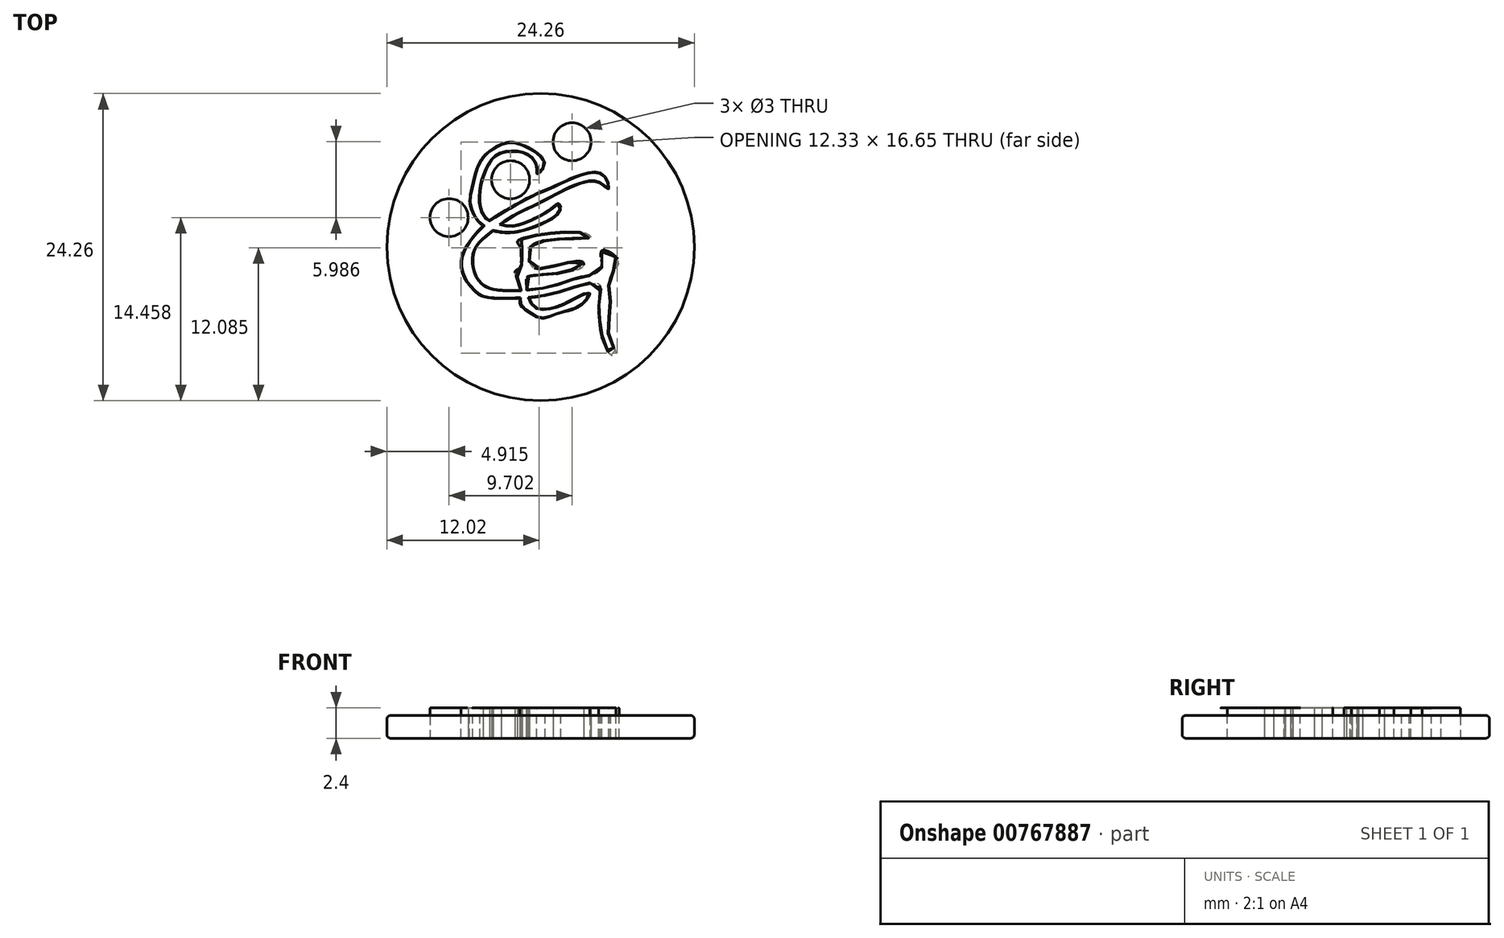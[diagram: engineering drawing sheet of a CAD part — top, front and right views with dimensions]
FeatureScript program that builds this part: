
annotation { "Feature Type Name" : "Feature", "Feature Type Description" : "" }
export const myFeature = defineFeature(function(context is Context, id is Id, definition is map)
    precondition{}
    {
        {
            var Q0;
            Q0=qCreatedBy(makeId("Top.planeOp"),FACE);
            var sketch = newSketch(context, id + "F0", { "sketchPlane" : qUnion([Q0])});
            skCircle(sketch, "E0", {"center": v(0, 0) * mm, "radius": 12.13 * mm});
            skCircle(sketch, "E1", {"center": v(-7.22, 2.33) * mm, "radius": 1.5 * mm});
            skCircle(sketch, "E2.1.0.0", {"center": v(-2.36, 5.32) * mm, "radius": 1.5 * mm});
            skCircle(sketch, "E2.2.0.0", {"center": v(2.49, 8.31) * mm, "radius": 1.5 * mm});
            skLineSegment(sketch, "E2.direction1", {"start": v(-7.22, 2.33) * mm, "end": v(-2.36, 5.32) * mm, "construction": true});
            skPoint(sketch, "E3.20.internal.snap0", {"position": v(-4.79, 3.82) * mm});
            skFitSpline(sketch, "E3", {"points": [v(-0.27, 5.8) * mm, v(0.34, 6.54) * mm, v(-0.62, 7.67) * mm, v(-1.5, 8.11) * mm, v(-2.55, 8.28) * mm, v(-4.1, 7.53) * mm, v(-4.89, 6.55) * mm, v(-5.26, 5.43) * mm, v(-5.52, 4.2) * mm, v(-5.57, 3.34) * mm, v(-4.72, 1.82) * mm, v(-2.7, 1.13) * mm, v(-0.35, 1.63) * mm, v(1.54, 2.89) * mm, v(1.42, 3.44) * mm, v(0.9, 3.08) * mm, v(-0.43, 2.3) * mm, v(-2.31, 1.67) * mm, v(-3.5, 1.92) * mm, v(-4.44, 2.44) * mm, v(-4.79, 4.2) * mm, v(-4.34, 6.01) * mm, v(-3.45, 7.26) * mm, v(-2.08, 7.54) * mm, v(-1.07, 7.32) * mm, v(-0.33, 6.4) * mm, v(-0.27, 5.8) * mm]});
            skFitSpline(sketch, "E4", {"points": [v(5.62, -8.55) * mm, v(5.96, -8.32) * mm, v(5.51, -7.5) * mm, v(5.44, -5.47) * mm, v(5.5, -4.03) * mm, v(5.54, -2.2) * mm, v(6.18, -1.14) * mm, v(4.94, -0.23) * mm, v(4.75, -0.7) * mm, v(4.84, -1.47) * mm, v(4.33, -2.02) * mm, v(2.9, -2.42) * mm, v(1.63, -2.84) * mm, v(0, -3.25) * mm, v(-2.31, -3.42) * mm, v(-4.24, -3.14) * mm, v(-5.19, -2) * mm, v(-5.23, -0.31) * mm, v(-4.32, 0.8) * mm, v(-2.31, 2.34) * mm, v(-0.27, 3.37) * mm, v(1.6, 4.35) * mm, v(3.38, 5.09) * mm, v(4.73, 5.03) * mm, v(5.38, 4.6) * mm, v(4.83, 5.8) * mm, v(1.54, 5.02) * mm, v(0.3, 4.49) * mm, v(-0.99, 3.9) * mm, v(-2.83, 2.87) * mm, v(-3.92, 2.18) * mm, v(-5.17, 1.02) * mm, v(-5.9, 0) * mm, v(-6.26, -1.03) * mm, v(-6.06, -2.32) * mm, v(-5.23, -3.45) * mm, v(-4.44, -3.94) * mm, v(-1.6, -4.03) * mm, v(1.43, -3.58) * mm, v(4.57, -2.9) * mm, v(4.6, -4.2) * mm, v(4.66, -5.96) * mm, v(4.86, -7.19) * mm, v(5.62, -8.55) * mm]});
            skFitSpline(sketch, "E5", {"points": [v(3.93, 0.77) * mm, v(2.32, 0.66) * mm, v(0.7, 0.53) * mm, v(-0.8, 0) * mm, v(-0.78, -1.37) * mm, v(0, -1.68) * mm, v(3.32, -1.16) * mm, v(3.23, -1.66) * mm, v(2.2, -1.85) * mm, v(1.22, -2.12) * mm, v(-0.87, -2.28) * mm, v(-1.13, -2.63) * mm, v(-0.75, -4.35) * mm, v(0, -4.89) * mm, v(1.52, -4.6) * mm, v(3.04, -3.85) * mm, v(3.88, -3.61) * mm, v(3.18, -4.6) * mm, v(1.49, -5.22) * mm, v(0, -5.63) * mm, v(-0.92, -5.13) * mm, v(-1.6, -4.56) * mm, v(-1.6, -3.13) * mm, v(-2, -1.92) * mm, v(-1.6, -1.59) * mm, v(-1.6, 0) * mm, v(-1.84, 0.36) * mm, v(-1.6, 0.63) * mm, v(3.48, 1.12) * mm, v(3.93, 0.77) * mm]});
            skSolve(sketch);
        }
        {
            var Q0;
            Q0=makeQuery(id+"F0.imprint","IMPRINT",FACE,{"disambiguationData":[TD([[makeQuery(id+"F0.imprint","IMPRINT",EDGE,{"derivedFrom":sQuery(id+"F0.wireOp",EDGE,"E2.1.0.0")}),1.0]])]});
            var Q1;
            Q1=makeQuery(id+"F0.imprint","IMPRINT",FACE,{"disambiguationData":[TD([[makeQuery(id+"F0.imprint","IMPRINT",EDGE,{"derivedFrom":sQuery(id+"F0.wireOp",EDGE,"E1")}),1.0]])]});
            var Q2;
            Q2=makeQuery(id+"F0.imprint","IMPRINT",FACE,{"disambiguationData":[TD([[makeQuery(id+"F0.imprint","IMPRINT",EDGE,{"derivedFrom":sQuery(id+"F0.wireOp",EDGE,"E2.2.0.0")}),1.0]])]});
            var Q3;
            {var subQ0=sQuery(id+"F0.wireOp",EDGE,"E4");var subQ1=sQuery(id+"F0.wireOp",EDGE,"E3");var subQ2=makeQuery(id+"F0.imprint","INTERSECT",VERTEX,{"disambiguationData":[OD(2.0)],"derivedFrom":[subQ1,subQ0]});Q3=makeQuery(id+"F0.imprint","IMPRINT",FACE,{"disambiguationData":[TD([[makeQuery(id+"F0.imprint","IMPRINT",EDGE,{"disambiguationData":[TD([[subQ2,-1.0]])],"derivedFrom":subQ1}),-1.0]])]});}
            var Q4;
            {var subQ0=sQuery(id+"F0.wireOp",EDGE,"E4");var subQ1=sQuery(id+"F0.wireOp",EDGE,"E3");var subQ2=makeQuery(id+"F0.imprint","INTERSECT",VERTEX,{"disambiguationData":[OD(0.0)],"derivedFrom":[subQ1,subQ0]});Q4=makeQuery(id+"F0.imprint","IMPRINT",FACE,{"disambiguationData":[TD([[makeQuery(id+"F0.imprint","IMPRINT",EDGE,{"disambiguationData":[TD([[subQ2,-1.0]])],"derivedFrom":subQ1}),1.0]])]});}
            var Q5;
            {var subQ0=sQuery(id+"F0.wireOp",EDGE,"E4");var subQ1=sQuery(id+"F0.wireOp",EDGE,"E3");var subQ2=makeQuery(id+"F0.imprint","INTERSECT",VERTEX,{"disambiguationData":[OD(0.0)],"derivedFrom":[subQ1,subQ0]});Q5=makeQuery(id+"F0.imprint","IMPRINT",FACE,{"disambiguationData":[TD([[makeQuery(id+"F0.imprint","IMPRINT",EDGE,{"disambiguationData":[TD([[subQ2,1.0]])],"derivedFrom":subQ1}),1.0]])]});}
            var Q6;
            {var subQ0=sQuery(id+"F0.wireOp",EDGE,"E4");var subQ1=sQuery(id+"F0.wireOp",EDGE,"E3");var subQ2=makeQuery(id+"F0.imprint","INTERSECT",VERTEX,{"disambiguationData":[OD(1.0)],"derivedFrom":[subQ1,subQ0]});Q6=makeQuery(id+"F0.imprint","IMPRINT",FACE,{"disambiguationData":[TD([[makeQuery(id+"F0.imprint","IMPRINT",EDGE,{"disambiguationData":[TD([[subQ2,1.0]])],"derivedFrom":subQ1}),1.0]])]});}
            var Q7;
            {var subQ0=sQuery(id+"F0.wireOp",EDGE,"E4");var subQ1=sQuery(id+"F0.wireOp",EDGE,"E3");var subQ2=makeQuery(id+"F0.imprint","INTERSECT",VERTEX,{"disambiguationData":[OD(0.0)],"derivedFrom":[subQ1,subQ0]});Q7=makeQuery(id+"F0.imprint","IMPRINT",FACE,{"disambiguationData":[TD([[makeQuery(id+"F0.imprint","IMPRINT",EDGE,{"disambiguationData":[TD([[subQ2,1.0]])],"derivedFrom":subQ1}),-1.0]])]});}
            var Q8;
            {var subQ0=sQuery(id+"F0.wireOp",EDGE,"E5");var subQ1=sQuery(id+"F0.wireOp",EDGE,"E4");var subQ2=makeQuery(id+"F0.imprint","INTERSECT",VERTEX,{"disambiguationData":[OD(0.0)],"derivedFrom":[subQ1,subQ0]});Q8=makeQuery(id+"F0.imprint","IMPRINT",FACE,{"disambiguationData":[TD([[makeQuery(id+"F0.imprint","IMPRINT",EDGE,{"disambiguationData":[TD([[subQ2,1.0]])],"derivedFrom":subQ1}),-1.0]])]});}
            var Q9;
            {var subQ0=sQuery(id+"F0.wireOp",EDGE,"E5");var subQ1=sQuery(id+"F0.wireOp",EDGE,"E4");var subQ2=makeQuery(id+"F0.imprint","INTERSECT",VERTEX,{"disambiguationData":[OD(1.0)],"derivedFrom":[subQ1,subQ0]});Q9=makeQuery(id+"F0.imprint","IMPRINT",FACE,{"disambiguationData":[TD([[makeQuery(id+"F0.imprint","IMPRINT",EDGE,{"disambiguationData":[TD([[subQ2,1.0]])],"derivedFrom":subQ1}),1.0]])]});}
            var Q10;
            {var subQ0=sQuery(id+"F0.wireOp",EDGE,"E5");var subQ1=sQuery(id+"F0.wireOp",EDGE,"E4");var subQ2=makeQuery(id+"F0.imprint","INTERSECT",VERTEX,{"disambiguationData":[OD(0.0)],"derivedFrom":[subQ1,subQ0]});Q10=makeQuery(id+"F0.imprint","IMPRINT",FACE,{"disambiguationData":[TD([[makeQuery(id+"F0.imprint","IMPRINT",EDGE,{"disambiguationData":[TD([[subQ2,1.0]])],"derivedFrom":subQ1}),1.0]])]});}
            var Q11;
            {var subQ0=sQuery(id+"F0.wireOp",EDGE,"E5");var subQ1=sQuery(id+"F0.wireOp",EDGE,"E4");var subQ2=makeQuery(id+"F0.imprint","INTERSECT",VERTEX,{"disambiguationData":[OD(2.0)],"derivedFrom":[subQ1,subQ0]});Q11=makeQuery(id+"F0.imprint","IMPRINT",FACE,{"disambiguationData":[TD([[makeQuery(id+"F0.imprint","IMPRINT",EDGE,{"disambiguationData":[TD([[subQ2,-1.0]])],"derivedFrom":subQ1}),-1.0]])]});}
            extrude(context, id + "F1", {"entities" : qUnion([Q0, Q1, Q2, Q3, Q4, Q5, Q6, Q7, Q8, Q9, Q10, Q11]), "depth" : 2.4 * mm, "offsetDistance" : 25 * mm});
        }
        {
            var Q0;
            Q0=makeQuery(id+"F0.imprint","IMPRINT",FACE,{"disambiguationData":[TD([[makeQuery(id+"F0.imprint","IMPRINT",EDGE,{"derivedFrom":sQuery(id+"F0.wireOp",EDGE,"E0")}),1.0]])]});
            extrude(context, id + "F2", {"entities" : qUnion([Q0]), "depth" : 1.8 * mm, "offsetDistance" : 25 * mm});
        }
        {
            var Q0;
            Q0=makeQuery(id+"F2.opExtrude","CAP_EDGE",EDGE,{"disambiguationData":[OSD([sQuery(id+"F0.wireOp",EDGE,"E0")])],"isStart":false});
            var Q1;
            Q1=makeQuery(id+"F2.opExtrude","CAP_EDGE",EDGE,{"disambiguationData":[OSD([sQuery(id+"F0.wireOp",EDGE,"E0")])],"isStart":true});
            fillet(context, id + "F3", {"entities" : qUnion([Q0, Q1]), "radius" : 0.3 * mm, "tangentPropagation" : true, "allowEdgeOverflow" : false});
        }
        {
            var Q0;
            Q0=makeQuery(id+"F1.opExtrude","CAP_FACE",FACE,{"disambiguationData":[OSD([sQuery(id+"F0.wireOp",EDGE,"E2.1.0.0")])],"isStart":false});
            var Q1;
            Q1=makeQuery(id+"F1.opExtrude","CAP_FACE",FACE,{"disambiguationData":[OSD([sQuery(id+"F0.wireOp",EDGE,"E2.2.0.0")])],"isStart":false});
            var Q2;
            Q2=makeQuery(id+"F1.opExtrude","CAP_FACE",FACE,{"disambiguationData":[OSD([sQuery(id+"F0.wireOp",EDGE,"E1")])],"isStart":false});
            var Q3;
            Q3=makeQuery(id+"F1.opExtrude","CAP_FACE",FACE,{"disambiguationData":[OSD([sQuery(id+"F0.wireOp",EDGE,"E3"),sQuery(id+"F0.wireOp",EDGE,"E4"),sQuery(id+"F0.wireOp",EDGE,"E5")])],"isStart":false});
            fillet(context, id + "F4", {"entities" : qUnion([Q0, Q1, Q2, Q3]), "radius" : 0.05 * mm, "tangentPropagation" : true, "allowEdgeOverflow" : false});
        }
    });
